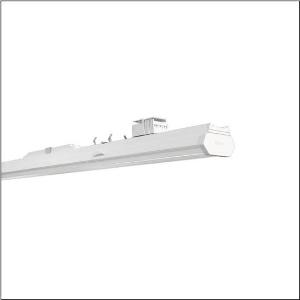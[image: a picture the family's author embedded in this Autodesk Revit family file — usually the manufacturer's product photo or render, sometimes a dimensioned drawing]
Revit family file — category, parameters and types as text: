
# Revit family: licross_11_protected_mo_51td11dn495g
name_source: partatom
category: Lighting Fixtures
units: mm (PartAtom-declared; Revit-internal decimal feet)

## family parameters
Cut with Voids When Loaded = No
Host = Face
Light Source = No
Part Type = Normal
Room Calculation Point = No
Round Connector Dimension = Use Diameter
Shared = No

## types (1)
- --- (1 x LED, 9930 lm, 57.1 W, 4000K)
    Apparent Load = 57 VA
    CIE Flux Codes = 83 94 98 100 100
    Color Rendering = 80
    Color Temperature = 4000K
    Default Elevation = 1800 mm
    Description = Licross 11 Protected MO, luminaire insert, of sheet steel, galvanised, coil coated, white, length: 1.500mm, width: 90mm, height: 101mm, LED rated luminous flux: 9.930lm, light colour: 840, SDCM (Standard Deviation of Colour Matching)MacAdam ≤ 2 SDCM (initial), control gear: DALI 2, with plug, 5-pole, with phase selection, mains connection: 220..240V, AC, 50/60Hz, rated input power: 57W, internal wiring halogen-free, primary light control with lens, of plastic, primary optical cover: cover, of PMMA, light emission: direct distribution, primary light characteristic: symmetric, protection rating (complete): IP54, insulation class (complete): insulation class I (protective earthing), certification: CE, ENEC, VDE, UKCA, protection symbol: D if used in an environment with non-conductive dust loads with corresponding accessories, impact resistance: IK06, permissible ambient temperature for indoor applications: -25..+35°C, corresponds to IFS (International Featured Standards) requirements for safety and quality in the food industry, reducing of maximum allowable ambient temperature of 5°C with ceiling mounting, LABS conformity tested according to VDMA 24364:2018-05, The light source and the operating device comply with the requirements of the Ecodesign Regulation (EU) 2019/2020 and are replaceable in accordance with this regulation, packaging unit: 1 piece
    Height = 92 mm
    Lamp = 1 x LED
    Lamp Light Flux = 9930 lm
    Lamp Power = 57.1 W
    Lamp count = 1
    Length = 1500 mm
    Luminous efficacy = 174 lm/W
    Manufacturer = Siteco
    ModVariant = No
    Model = 51TD11DN495G
    Mounting Place = Ceiling
    Mounting Type = Pendant
    Number of Poles = 1
    OnlyDefault = Yes
    Power Factor = 1
    Product Name = Licross 11 Protected MO
    Product group = luminaire insert | ceiling pendant
    ProductGroupID = 901
    Protection Class = Protection class I
    Protection Degree = IP 54
    RLX_Detail_Level = 1
    RLX_Emergency_Light_Flux = 0 lm
    RLX_Emergency_Type = 0
    RLX_Emergency_Type_DB = No
    RlxData = <blob elided: 24437 chars, md5=96507c57>
    Socket = socket
    Standby Power = 0 W
    System Light Flux = 9930 lm
    System Power = 57 W
    Type Comments = factory setting: luminous flux: 100 % | dim-lin: 254 | 378 mA
    Type Image = l_1256145.jpg
    URL = http://relux.com
    VarID = @adj_104113
    Voltage = 0 V
    Weight = 0.00 kg
    Width = 88 mm

## geometry (parser evidence)
native form markers: Blend x4, Sweep x10
no freeform markers — native parametric forms only
